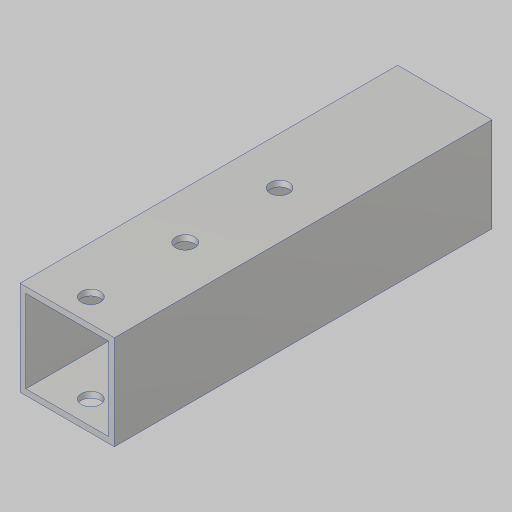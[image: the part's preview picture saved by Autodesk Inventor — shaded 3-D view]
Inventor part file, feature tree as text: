
AUTODESK INVENTOR PART (.ipt)
format: ipt  version: 2023.5 (Build 275446000, 446)  size: 112,640 bytes
history: native  units: in
note: dims shown in document units (in); Inventor stores cm internally (conversion verified against a paired STEP export)
features: sketch x2, extrude x1, hole x1
ambient origin geometry x8: Origin, YZ Plane, XZ Plane, XY Plane, X Axis, Y Axis, Z Axis, Center Point
bodies: Solid1 (feature_tree)
feature tree (4):
  extrude  "Extrusion1"  Depth=1.0in
  hole  "Hole1"  [1 undecoded]
  sketch  "Sketch1"  dims[d0=1.0in d1=1.0in]
  sketch  "Sketch2"  dims[d3=0.875in d4=0.875in d5=4.0in d6=0.0in d7=0.25in d8=1.0in d9=1.0in d10=0.201in d11=0.75in d12=0.385in d13=0.25in d14=0.5635in d15=1.0in d16=0.8108in]
note: 1 required parameter value undecoded (feature->parameter linkage not recoverable at this tier; creation-order binding heuristic only, values carry confidence <= 0.55)
